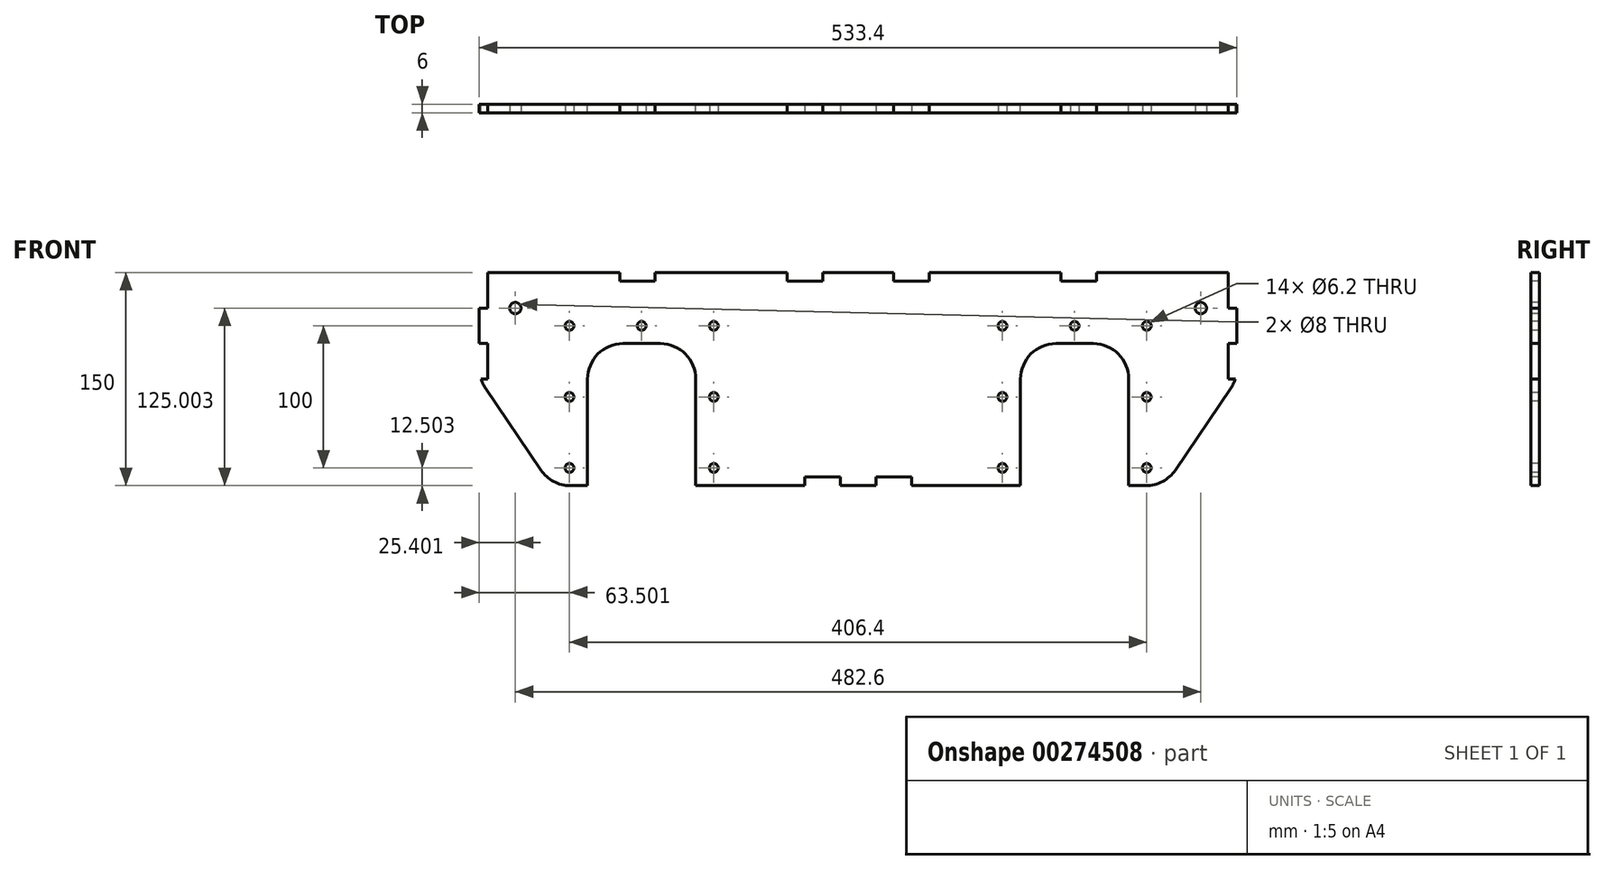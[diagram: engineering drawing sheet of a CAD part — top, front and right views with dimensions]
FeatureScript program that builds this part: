
annotation { "Feature Type Name" : "Feature", "Feature Type Description" : "" }
export const myFeature = defineFeature(function(context is Context, id is Id, definition is map)
    precondition{}
    {
        {
            var Q0;
            Q0=qCreatedBy(makeId("Front.planeOp"),FACE);
            var sketch = newSketch(context, id + "F0", { "sketchPlane" : qUnion([Q0])});
            skLineSegment(sketch, "E0", {"start": v(-308.6, 50.95) * mm, "end": v(224.8, 50.95) * mm});
            skLineSegment(sketch, "E1", {"start": v(224.8, 50.95) * mm, "end": v(224.8, -16.38) * mm});
            skLineSegment(sketch, "E2", {"start": v(220.5, -30.4) * mm, "end": v(181.44, -88.07) * mm});
            skLineSegment(sketch, "E3", {"start": v(160.74, -99.05) * mm, "end": v(148.6, -99.05) * mm});
            skLineSegment(sketch, "E4", {"start": v(148.6, -99.05) * mm, "end": v(148.6, -24.05) * mm});
            skLineSegment(sketch, "E5", {"start": v(123.6, 0.95) * mm, "end": v(97.4, 0.95) * mm});
            skLineSegment(sketch, "E6", {"start": v(72.4, -24.05) * mm, "end": v(72.4, -99.05) * mm});
            skLineSegment(sketch, "E7", {"start": v(72.4, -99.05) * mm, "end": v(-156.2, -99.05) * mm});
            skLineSegment(sketch, "E8", {"start": v(-156.2, -99.05) * mm, "end": v(-156.2, -24.05) * mm});
            skLineSegment(sketch, "E9", {"start": v(-181.2, 0.95) * mm, "end": v(-207.4, 0.95) * mm});
            skLineSegment(sketch, "E10", {"start": v(-232.4, -24.05) * mm, "end": v(-232.4, -99.05) * mm});
            skLineSegment(sketch, "E11", {"start": v(-232.4, -99.05) * mm, "end": v(-244.54, -99.05) * mm});
            skLineSegment(sketch, "E12", {"start": v(-265.24, -88.07) * mm, "end": v(-304.3, -30.4) * mm});
            skLineSegment(sketch, "E13", {"start": v(-308.6, -16.38) * mm, "end": v(-308.6, 50.95) * mm});
            skPoint(sketch, "E14.visualSharp", {"position": v(-257.8, -99.05) * mm});
            skArc(sketch, "E14.filletArc", {"start": v(-265.24, -88.07) * mm, "mid": v(-256.25, -96.13) * mm, "end": v(-244.54, -99.05) * mm});
            skPoint(sketch, "E15.visualSharp", {"position": v(-308.6, -24.05) * mm});
            skArc(sketch, "E15.filletArc", {"start": v(-308.6, -16.38) * mm, "mid": v(-307.5, -23.7) * mm, "end": v(-304.3, -30.4) * mm});
            skPoint(sketch, "E16.visualSharp", {"position": v(-232.4, 0.95) * mm});
            skArc(sketch, "E16.filletArc", {"start": v(-207.4, 0.95) * mm, "mid": v(-225.08, -6.37) * mm, "end": v(-232.4, -24.05) * mm});
            skPoint(sketch, "E17.visualSharp", {"position": v(-156.2, 0.95) * mm});
            skArc(sketch, "E17.filletArc", {"start": v(-156.2, -24.05) * mm, "mid": v(-163.52, -6.37) * mm, "end": v(-181.2, 0.95) * mm});
            skPoint(sketch, "E18.visualSharp", {"position": v(72.4, 0.95) * mm});
            skArc(sketch, "E18.filletArc", {"start": v(97.4, 0.95) * mm, "mid": v(79.72, -6.37) * mm, "end": v(72.4, -24.05) * mm});
            skPoint(sketch, "E19.visualSharp", {"position": v(148.6, 0.95) * mm});
            skArc(sketch, "E19.filletArc", {"start": v(148.6, -24.05) * mm, "mid": v(141.28, -6.37) * mm, "end": v(123.6, 0.95) * mm});
            skPoint(sketch, "E20.visualSharp", {"position": v(174, -99.05) * mm});
            skArc(sketch, "E20.filletArc", {"start": v(160.74, -99.05) * mm, "mid": v(172.45, -96.13) * mm, "end": v(181.44, -88.07) * mm});
            skPoint(sketch, "E21.visualSharp", {"position": v(224.8, -24.05) * mm});
            skArc(sketch, "E21.filletArc", {"start": v(220.5, -30.4) * mm, "mid": v(223.7, -23.7) * mm, "end": v(224.8, -16.38) * mm});
            skSolve(sketch);
        }
        {
            var Q0;
            Q0 = qSketchRegion(id + "F0", true);
            extrude(context, id + "F1", {"entities" : qUnion([Q0]), "depth" : 6 * mm});
        }
        {
            var Q0;
            Q0=makeQuery(id+"F1.opExtrude","CAP_FACE",FACE,{"disambiguationData":[OSD([sQuery(id+"F0.wireOp",EDGE,"E0"),sQuery(id+"F0.wireOp",EDGE,"E1"),sQuery(id+"F0.wireOp",EDGE,"E2"),sQuery(id+"F0.wireOp",EDGE,"E3"),sQuery(id+"F0.wireOp",EDGE,"E4"),sQuery(id+"F0.wireOp",EDGE,"E5"),sQuery(id+"F0.wireOp",EDGE,"E6"),sQuery(id+"F0.wireOp",EDGE,"E7"),sQuery(id+"F0.wireOp",EDGE,"E8"),sQuery(id+"F0.wireOp",EDGE,"E9"),sQuery(id+"F0.wireOp",EDGE,"E10"),sQuery(id+"F0.wireOp",EDGE,"E11"),sQuery(id+"F0.wireOp",EDGE,"E12"),sQuery(id+"F0.wireOp",EDGE,"E13"),sQuery(id+"F0.wireOp",EDGE,"E14.filletArc"),sQuery(id+"F0.wireOp",EDGE,"E15.filletArc"),sQuery(id+"F0.wireOp",EDGE,"E16.filletArc"),sQuery(id+"F0.wireOp",EDGE,"E17.filletArc"),sQuery(id+"F0.wireOp",EDGE,"E18.filletArc"),sQuery(id+"F0.wireOp",EDGE,"E19.filletArc"),sQuery(id+"F0.wireOp",EDGE,"E20.filletArc"),sQuery(id+"F0.wireOp",EDGE,"E21.filletArc")])],"isStart":false});
            var sketch = newSketch(context, id + "F2", { "sketchPlane" : qUnion([Q0])});
            skLineSegment(sketch, "E22.bottom", {"start": v(-308.6, 50.95) * mm, "end": v(-302.6, 50.95) * mm});
            skLineSegment(sketch, "E22.top", {"start": v(-308.6, 25.95) * mm, "end": v(-302.6, 25.95) * mm});
            skLineSegment(sketch, "E22.left", {"start": v(-308.6, 50.95) * mm, "end": v(-308.6, 25.95) * mm});
            skLineSegment(sketch, "E22.right", {"start": v(-302.6, 50.95) * mm, "end": v(-302.6, 25.95) * mm});
            skLineSegment(sketch, "E23.bottom", {"start": v(-308.6, 0.95) * mm, "end": v(-302.6, 0.95) * mm});
            skLineSegment(sketch, "E23.top", {"start": v(-308.6, -24.05) * mm, "end": v(-302.6, -24.05) * mm});
            skLineSegment(sketch, "E23.left", {"start": v(-308.6, 0.95) * mm, "end": v(-308.6, -24.05) * mm});
            skLineSegment(sketch, "E23.right", {"start": v(-302.6, 0.95) * mm, "end": v(-302.6, -24.05) * mm});
            skLineSegment(sketch, "E24.bottom", {"start": v(224.8, 50.95) * mm, "end": v(218.8, 50.95) * mm});
            skLineSegment(sketch, "E24.left", {"start": v(224.8, 50.95) * mm, "end": v(224.8, 25.95) * mm});
            skLineSegment(sketch, "E24.right", {"start": v(218.8, 50.95) * mm, "end": v(218.8, 25.95) * mm});
            skLineSegment(sketch, "E25.bottom", {"start": v(224.8, 0.95) * mm, "end": v(218.8, 0.95) * mm});
            skLineSegment(sketch, "E25.top", {"start": v(224.8, -24.05) * mm, "end": v(218.8, -24.05) * mm});
            skLineSegment(sketch, "E25.left", {"start": v(224.8, 0.95) * mm, "end": v(224.8, -24.05) * mm});
            skLineSegment(sketch, "E25.right", {"start": v(218.8, 0.95) * mm, "end": v(218.8, -24.05) * mm});
            skLineSegment(sketch, "E26", {"start": v(218.8, 25.95) * mm, "end": v(224.8, 25.95) * mm});
            skLineSegment(sketch, "E27.bottom", {"start": v(-79.4, -99.05) * mm, "end": v(-54.4, -99.05) * mm});
            skLineSegment(sketch, "E27.top", {"start": v(-79.4, -93.05) * mm, "end": v(-54.4, -93.05) * mm});
            skLineSegment(sketch, "E27.left", {"start": v(-79.4, -99.05) * mm, "end": v(-79.4, -93.05) * mm});
            skLineSegment(sketch, "E27.right", {"start": v(-54.4, -99.05) * mm, "end": v(-54.4, -93.05) * mm});
            skLineSegment(sketch, "E28.bottom", {"start": v(-29.4, -99.05) * mm, "end": v(-4.4, -99.05) * mm});
            skLineSegment(sketch, "E28.top", {"start": v(-29.4, -93.05) * mm, "end": v(-4.4, -93.05) * mm});
            skLineSegment(sketch, "E28.left", {"start": v(-29.4, -99.05) * mm, "end": v(-29.4, -93.05) * mm});
            skLineSegment(sketch, "E28.right", {"start": v(-4.4, -99.05) * mm, "end": v(-4.4, -93.05) * mm});
            skLineSegment(sketch, "E29.bottom", {"start": v(-91.9, 50.95) * mm, "end": v(-66.9, 50.95) * mm});
            skLineSegment(sketch, "E29.top", {"start": v(-91.9, 44.95) * mm, "end": v(-66.9, 44.95) * mm});
            skLineSegment(sketch, "E29.left", {"start": v(-91.9, 50.95) * mm, "end": v(-91.9, 44.95) * mm});
            skLineSegment(sketch, "E29.right", {"start": v(-66.9, 50.95) * mm, "end": v(-66.9, 44.95) * mm});
            skLineSegment(sketch, "E30.bottom", {"start": v(-16.9, 50.95) * mm, "end": v(8.1, 50.95) * mm});
            skLineSegment(sketch, "E30.top", {"start": v(-16.9, 44.95) * mm, "end": v(8.1, 44.95) * mm});
            skLineSegment(sketch, "E30.left", {"start": v(-16.9, 50.95) * mm, "end": v(-16.9, 44.95) * mm});
            skLineSegment(sketch, "E30.right", {"start": v(8.1, 50.95) * mm, "end": v(8.1, 44.95) * mm});
            skLineSegment(sketch, "E31.bottom", {"start": v(-209.75, 50.95) * mm, "end": v(-184.75, 50.95) * mm});
            skLineSegment(sketch, "E31.top", {"start": v(-209.75, 44.95) * mm, "end": v(-184.75, 44.95) * mm});
            skLineSegment(sketch, "E31.left", {"start": v(-209.75, 50.95) * mm, "end": v(-209.75, 44.95) * mm});
            skLineSegment(sketch, "E31.right", {"start": v(-184.75, 50.95) * mm, "end": v(-184.75, 44.95) * mm});
            skLineSegment(sketch, "E32.bottom", {"start": v(100.95, 50.95) * mm, "end": v(125.95, 50.95) * mm});
            skLineSegment(sketch, "E32.top", {"start": v(100.95, 44.95) * mm, "end": v(125.95, 44.95) * mm});
            skLineSegment(sketch, "E32.left", {"start": v(100.95, 50.95) * mm, "end": v(100.95, 44.95) * mm});
            skLineSegment(sketch, "E32.right", {"start": v(125.95, 50.95) * mm, "end": v(125.95, 44.95) * mm});
            skSolve(sketch);
        }
        {
            var Q0;
            Q0 = qSketchRegion(id + "F2", true);
            extrude(context, id + "F3", {"entities" : qUnion([Q0]), "operationType" : NewBodyOperationType.REMOVE, "oppositeDirection" : true, "depth" : 25 * mm});
        }
        {
            var Q0;
            Q0=makeQuery(id+"F1.opExtrude","CAP_FACE",FACE,{"disambiguationData":[OSD([sQuery(id+"F0.wireOp",EDGE,"E0"),sQuery(id+"F0.wireOp",EDGE,"E1"),sQuery(id+"F0.wireOp",EDGE,"E2"),sQuery(id+"F0.wireOp",EDGE,"E3"),sQuery(id+"F0.wireOp",EDGE,"E4"),sQuery(id+"F0.wireOp",EDGE,"E5"),sQuery(id+"F0.wireOp",EDGE,"E6"),sQuery(id+"F0.wireOp",EDGE,"E7"),sQuery(id+"F0.wireOp",EDGE,"E8"),sQuery(id+"F0.wireOp",EDGE,"E9"),sQuery(id+"F0.wireOp",EDGE,"E10"),sQuery(id+"F0.wireOp",EDGE,"E11"),sQuery(id+"F0.wireOp",EDGE,"E12"),sQuery(id+"F0.wireOp",EDGE,"E13"),sQuery(id+"F0.wireOp",EDGE,"E14.filletArc"),sQuery(id+"F0.wireOp",EDGE,"E15.filletArc"),sQuery(id+"F0.wireOp",EDGE,"E16.filletArc"),sQuery(id+"F0.wireOp",EDGE,"E17.filletArc"),sQuery(id+"F0.wireOp",EDGE,"E18.filletArc"),sQuery(id+"F0.wireOp",EDGE,"E19.filletArc"),sQuery(id+"F0.wireOp",EDGE,"E20.filletArc"),sQuery(id+"F0.wireOp",EDGE,"E21.filletArc")])],"isStart":false});
            var sketch = newSketch(context, id + "F4", { "sketchPlane" : qUnion([Q0])});
            skPoint(sketch, "E33", {"position": v(-245.1, -86.55) * mm});
            skPoint(sketch, "E34", {"position": v(-245.1, -36.55) * mm});
            skPoint(sketch, "E35", {"position": v(-245.1, 13.45) * mm});
            skPoint(sketch, "E36", {"position": v(-143.5, 13.45) * mm});
            skPoint(sketch, "E37", {"position": v(-143.5, -36.55) * mm});
            skPoint(sketch, "E38", {"position": v(-143.5, -86.55) * mm});
            skPoint(sketch, "E39", {"position": v(-194.3, 13.45) * mm});
            skPoint(sketch, "E39.positionSnap0", {"position": v(-194.3, 0.95) * mm});
            skPoint(sketch, "E40", {"position": v(-283.2, 25.95) * mm});
            skLineSegment(sketch, "E41", {"start": v(-41.9, -99.05) * mm, "end": v(-41.9, 50.95) * mm});
            skPoint(sketch, "E42.MirrorP", {"position": v(199.4, 25.95) * mm});
            skPoint(sketch, "E43.MirrorP", {"position": v(110.5, 0.95) * mm});
            skPoint(sketch, "E44.MirrorP", {"position": v(161.3, 13.45) * mm});
            skPoint(sketch, "E45.MirrorP", {"position": v(110.5, 13.45) * mm});
            skPoint(sketch, "E46.MirrorP", {"position": v(59.7, 13.45) * mm});
            skPoint(sketch, "E47.MirrorP", {"position": v(161.3, -36.55) * mm});
            skPoint(sketch, "E48.MirrorP", {"position": v(161.3, -86.55) * mm});
            skPoint(sketch, "E49.MirrorP", {"position": v(59.7, -86.55) * mm});
            skPoint(sketch, "E50.MirrorP", {"position": v(59.7, -36.55) * mm});
            skSolve(sketch);
        }
        {
            var Q0;
            Q0=sQuery(id+"F4.wireOp",VERTEX,"E33");
            var Q1;
            Q1=sQuery(id+"F4.wireOp",VERTEX,"E34");
            var Q2;
            Q2=sQuery(id+"F4.wireOp",VERTEX,"E35");
            var Q3;
            Q3=sQuery(id+"F4.wireOp",VERTEX,"E39");
            var Q4;
            Q4=sQuery(id+"F4.wireOp",VERTEX,"E36");
            var Q5;
            Q5=sQuery(id+"F4.wireOp",VERTEX,"E37");
            var Q6;
            Q6=sQuery(id+"F4.wireOp",VERTEX,"E38");
            var Q7;
            Q7=sQuery(id+"F4.wireOp",VERTEX,"E49.MirrorP");
            var Q8;
            Q8=sQuery(id+"F4.wireOp",VERTEX,"E50.MirrorP");
            var Q9;
            Q9=sQuery(id+"F4.wireOp",VERTEX,"E46.MirrorP");
            var Q10;
            Q10=sQuery(id+"F4.wireOp",VERTEX,"E45.MirrorP");
            var Q11;
            Q11=sQuery(id+"F4.wireOp",VERTEX,"E44.MirrorP");
            var Q12;
            Q12=sQuery(id+"F4.wireOp",VERTEX,"E47.MirrorP");
            var Q13;
            Q13=sQuery(id+"F4.wireOp",VERTEX,"E48.MirrorP");
            var Q14;
            Q14=makeQuery(id+"F1.opExtrude","SWEPT_BODY",BODY,{"disambiguationData":[OSD([sQuery(id+"F0.wireOp",EDGE,"E0"),sQuery(id+"F0.wireOp",EDGE,"E1"),sQuery(id+"F0.wireOp",EDGE,"E2"),sQuery(id+"F0.wireOp",EDGE,"E3"),sQuery(id+"F0.wireOp",EDGE,"E4"),sQuery(id+"F0.wireOp",EDGE,"E5"),sQuery(id+"F0.wireOp",EDGE,"E6"),sQuery(id+"F0.wireOp",EDGE,"E7"),sQuery(id+"F0.wireOp",EDGE,"E8"),sQuery(id+"F0.wireOp",EDGE,"E9"),sQuery(id+"F0.wireOp",EDGE,"E10"),sQuery(id+"F0.wireOp",EDGE,"E11"),sQuery(id+"F0.wireOp",EDGE,"E12"),sQuery(id+"F0.wireOp",EDGE,"E13"),sQuery(id+"F0.wireOp",EDGE,"E14.filletArc"),sQuery(id+"F0.wireOp",EDGE,"E15.filletArc"),sQuery(id+"F0.wireOp",EDGE,"E16.filletArc"),sQuery(id+"F0.wireOp",EDGE,"E17.filletArc"),sQuery(id+"F0.wireOp",EDGE,"E18.filletArc"),sQuery(id+"F0.wireOp",EDGE,"E19.filletArc"),sQuery(id+"F0.wireOp",EDGE,"E20.filletArc"),sQuery(id+"F0.wireOp",EDGE,"E21.filletArc")])]});
            hole(context, id + "F5", {"style" : HoleStyle.SIMPLE, "endStyle" : HoleEndStyle.THROUGH, "standardTappedOrClearance" : lookupTablePath({ "standard" : "ISO", "size" : "6.2", "type" : "Drilled" }), "standardBlindInLast" : lookupTablePath({ "standard" : "ISO", "size" : "6.2", "type" : "Drilled" }), "holeDiameter" : 6.2 * mm, "tappedDepth" : 12 * mm, "tapClearance" : 3, "locations" : qUnion([Q0, Q1, Q2, Q3, Q4, Q5, Q6, Q7, Q8, Q9, Q10, Q11, Q12, Q13]), "scope" : qUnion([Q14])});
        }
        {
            var Q0;
            Q0=sQuery(id+"F4.wireOp",VERTEX,"E40");
            var Q1;
            Q1=sQuery(id+"F4.wireOp",VERTEX,"E42.MirrorP");
            var Q2;
            Q2=makeQuery(id+"F1.opExtrude","SWEPT_BODY",BODY,{"disambiguationData":[OSD([sQuery(id+"F0.wireOp",EDGE,"E0"),sQuery(id+"F0.wireOp",EDGE,"E1"),sQuery(id+"F0.wireOp",EDGE,"E2"),sQuery(id+"F0.wireOp",EDGE,"E3"),sQuery(id+"F0.wireOp",EDGE,"E4"),sQuery(id+"F0.wireOp",EDGE,"E5"),sQuery(id+"F0.wireOp",EDGE,"E6"),sQuery(id+"F0.wireOp",EDGE,"E7"),sQuery(id+"F0.wireOp",EDGE,"E8"),sQuery(id+"F0.wireOp",EDGE,"E9"),sQuery(id+"F0.wireOp",EDGE,"E10"),sQuery(id+"F0.wireOp",EDGE,"E11"),sQuery(id+"F0.wireOp",EDGE,"E12"),sQuery(id+"F0.wireOp",EDGE,"E13"),sQuery(id+"F0.wireOp",EDGE,"E14.filletArc"),sQuery(id+"F0.wireOp",EDGE,"E15.filletArc"),sQuery(id+"F0.wireOp",EDGE,"E16.filletArc"),sQuery(id+"F0.wireOp",EDGE,"E17.filletArc"),sQuery(id+"F0.wireOp",EDGE,"E18.filletArc"),sQuery(id+"F0.wireOp",EDGE,"E19.filletArc"),sQuery(id+"F0.wireOp",EDGE,"E20.filletArc"),sQuery(id+"F0.wireOp",EDGE,"E21.filletArc")])]});
            hole(context, id + "F6", {"style" : HoleStyle.SIMPLE, "endStyle" : HoleEndStyle.THROUGH, "standardTappedOrClearance" : lookupTablePath({ "standard" : "ISO", "size" : "8", "type" : "Drilled" }), "standardBlindInLast" : lookupTablePath({ "standard" : "ISO", "size" : "8", "type" : "Drilled" }), "holeDiameter" : 8 * mm, "tappedDepth" : 12 * mm, "tapClearance" : 3, "locations" : qUnion([Q0, Q1]), "scope" : qUnion([Q2])});
        }
    });
